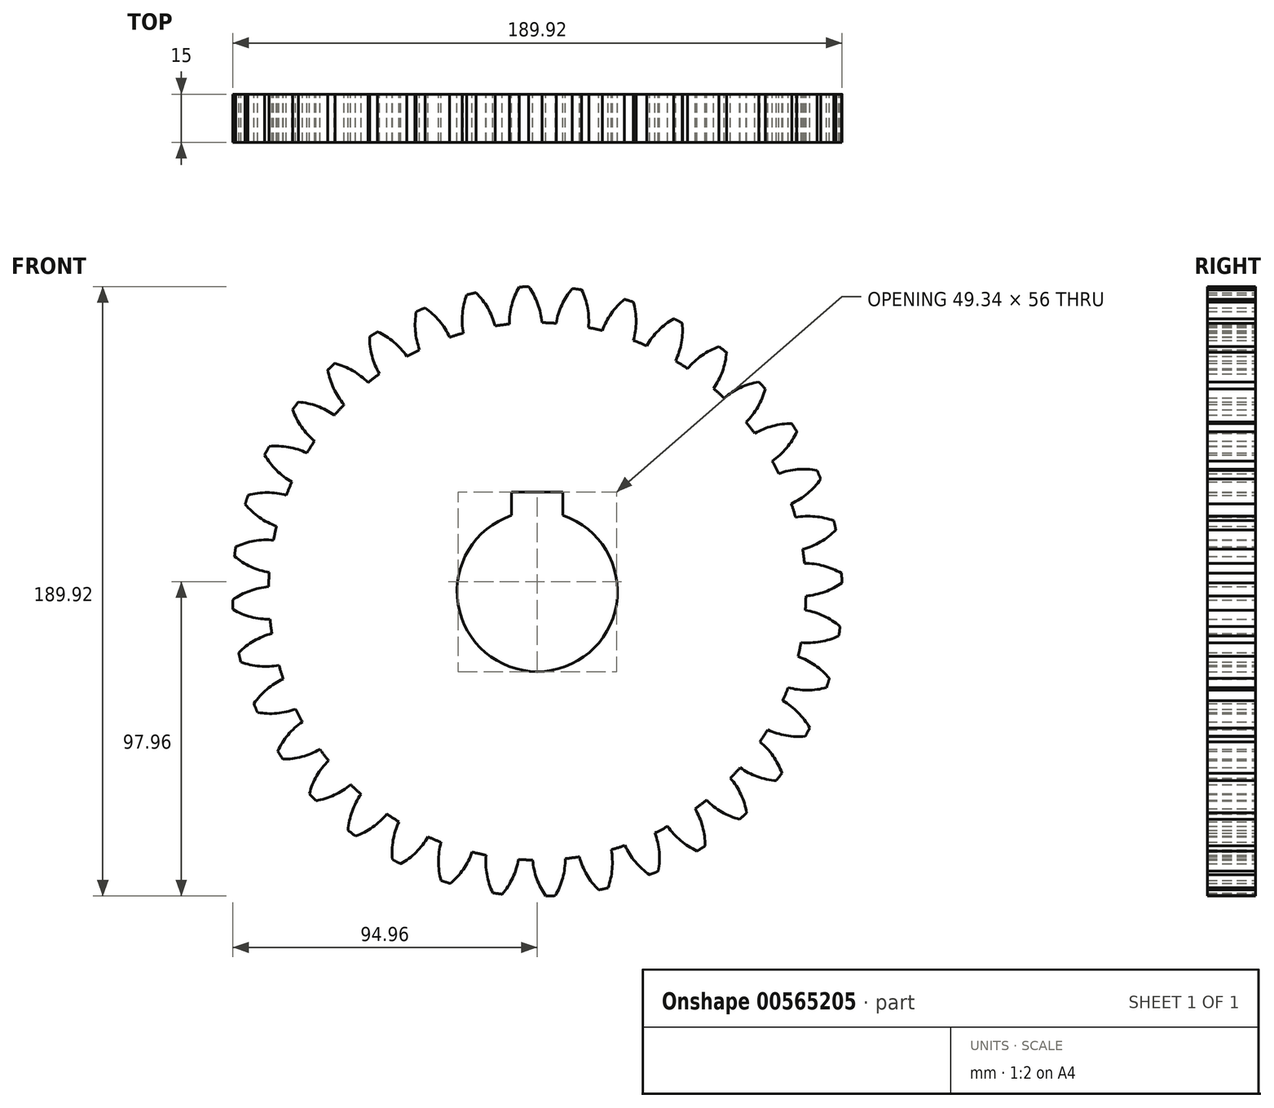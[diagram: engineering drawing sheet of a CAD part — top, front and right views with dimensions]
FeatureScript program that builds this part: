
annotation { "Feature Type Name" : "Feature", "Feature Type Description" : "" }
export const myFeature = defineFeature(function(context is Context, id is Id, definition is map)
    precondition{}
    {
        {
            var Q0;
            Q0=qCreatedBy(makeId("Front.planeOp"),FACE);
            var sketch = newSketch(context, id + "F0", { "sketchPlane" : qUnion([Q0])});
            skCircle(sketch, "E0", {"center": v(0, 0) * mm, "radius": 83.75 * mm});
            skCircle(sketch, "E1", {"center": v(0, 0) * mm, "radius": 90 * mm, "construction": true});
            skCircle(sketch, "E2", {"center": v(0, 0) * mm, "radius": 95 * mm, "construction": true});
            skLineSegment(sketch, "E3", {"start": v(0, 0) * mm, "end": v(0, 97.65) * mm, "construction": true});
            skLineSegment(sketch, "E4", {"start": v(0, 0) * mm, "end": v(-7.83, 179.33) * mm, "construction": true});
            skLineSegment(sketch, "E5", {"start": v(0, 90) * mm, "end": v(-217.65, 90) * mm, "construction": true});
            skLineSegment(sketch, "E6", {"start": v(0, 90) * mm, "end": v(-200.71, 16.95) * mm, "construction": true});
            skCircle(sketch, "E7", {"center": v(0, 0) * mm, "radius": 84.57 * mm, "construction": true});
            skCircle(sketch, "E8", {"center": v(0, 90) * mm, "radius": 22.5 * mm, "construction": true});
            skArc(sketch, "E9", {"start": v(0, 90) * mm, "mid": v(-1.18, 92.57) * mm, "end": v(-2.66, 94.96) * mm});
            skArc(sketch, "E10", {"start": v(1.43, 83.74) * mm, "mid": v(0.94, 86.92) * mm, "end": v(0, 90) * mm});
            skArc(sketch, "E11.MirrorCS", {"start": v(-8.72, 83.3) * mm, "mid": v(-8.5, 86.5) * mm, "end": v(-7.84, 89.66) * mm});
            skArc(sketch, "E12.MirrorCS", {"start": v(-7.84, 89.66) * mm, "mid": v(-6.9, 92.32) * mm, "end": v(-5.62, 94.83) * mm});
            skArc(sketch, "E13", {"start": v(-5.62, 94.83) * mm, "mid": v(-4.14, 94.9) * mm, "end": v(-2.66, 94.96) * mm});
            skSolve(sketch);
        }
        {
            var Q0;
            Q0=qSketchRegion(id+"F0",true);
            extrude(context, id + "F1", {"entities" : qUnion([Q0]), "depth" : 15 * mm, "offsetDistance" : 25.4 * mm});
        }
        {
            var Q0;
            Q0=makeQuery(id+"F1.opExtrude","SWEPT_BODY",BODY,{"disambiguationData":[OSD([sQuery(id+"F0.wireOp",EDGE,"E0"),sQuery(id+"F0.wireOp",EDGE,"E9"),sQuery(id+"F0.wireOp",EDGE,"E10"),sQuery(id+"F0.wireOp",EDGE,"E11.MirrorCS"),sQuery(id+"F0.wireOp",EDGE,"E12.MirrorCS"),sQuery(id+"F0.wireOp",EDGE,"E13")])]});
            var Q1;
            Q1=makeQuery(id+"F1.opExtrude","SWEPT_FACE",FACE,{"disambiguationData":[OSD([sQuery(id+"F0.wireOp",EDGE,"E0")])]});
            circularPattern(context, id + "F2", {"entities" : qUnion([Q0]), "axis" : qUnion([Q1]), "angle" : 360 * degree, "instanceCount" : 36, "equalSpace" : true});
        }
        {
            var Q0;
            Q0=makeQuery(id+"F2.opPattern","COPY",BODY,{"derivedFrom":makeQuery(id+"F1.opExtrude","SWEPT_BODY",BODY,{"disambiguationData":[OSD([sQuery(id+"F0.wireOp",EDGE,"E0"),sQuery(id+"F0.wireOp",EDGE,"E9"),sQuery(id+"F0.wireOp",EDGE,"E10"),sQuery(id+"F0.wireOp",EDGE,"E11.MirrorCS"),sQuery(id+"F0.wireOp",EDGE,"E12.MirrorCS"),sQuery(id+"F0.wireOp",EDGE,"E13")])]}),"instanceName":"17"});
            var Q1;
            Q1=makeQuery(id+"F2.opPattern","COPY",BODY,{"derivedFrom":makeQuery(id+"F1.opExtrude","SWEPT_BODY",BODY,{"disambiguationData":[OSD([sQuery(id+"F0.wireOp",EDGE,"E0"),sQuery(id+"F0.wireOp",EDGE,"E9"),sQuery(id+"F0.wireOp",EDGE,"E10"),sQuery(id+"F0.wireOp",EDGE,"E11.MirrorCS"),sQuery(id+"F0.wireOp",EDGE,"E12.MirrorCS"),sQuery(id+"F0.wireOp",EDGE,"E13")])]}),"instanceName":"13"});
            var Q2;
            Q2=makeQuery(id+"F1.opExtrude","SWEPT_BODY",BODY,{"disambiguationData":[OSD([sQuery(id+"F0.wireOp",EDGE,"E0"),sQuery(id+"F0.wireOp",EDGE,"E9"),sQuery(id+"F0.wireOp",EDGE,"E10"),sQuery(id+"F0.wireOp",EDGE,"E11.MirrorCS"),sQuery(id+"F0.wireOp",EDGE,"E12.MirrorCS"),sQuery(id+"F0.wireOp",EDGE,"E13")])]});
            var Q3;
            Q3=makeQuery(id+"F2.opPattern","COPY",BODY,{"derivedFrom":makeQuery(id+"F1.opExtrude","SWEPT_BODY",BODY,{"disambiguationData":[OSD([sQuery(id+"F0.wireOp",EDGE,"E0"),sQuery(id+"F0.wireOp",EDGE,"E9"),sQuery(id+"F0.wireOp",EDGE,"E10"),sQuery(id+"F0.wireOp",EDGE,"E11.MirrorCS"),sQuery(id+"F0.wireOp",EDGE,"E12.MirrorCS"),sQuery(id+"F0.wireOp",EDGE,"E13")])]}),"instanceName":"7"});
            var Q4;
            Q4=makeQuery(id+"F2.opPattern","COPY",BODY,{"derivedFrom":makeQuery(id+"F1.opExtrude","SWEPT_BODY",BODY,{"disambiguationData":[OSD([sQuery(id+"F0.wireOp",EDGE,"E0"),sQuery(id+"F0.wireOp",EDGE,"E9"),sQuery(id+"F0.wireOp",EDGE,"E10"),sQuery(id+"F0.wireOp",EDGE,"E11.MirrorCS"),sQuery(id+"F0.wireOp",EDGE,"E12.MirrorCS"),sQuery(id+"F0.wireOp",EDGE,"E13")])]}),"instanceName":"18"});
            var Q5;
            Q5=makeQuery(id+"F2.opPattern","COPY",BODY,{"derivedFrom":makeQuery(id+"F1.opExtrude","SWEPT_BODY",BODY,{"disambiguationData":[OSD([sQuery(id+"F0.wireOp",EDGE,"E0"),sQuery(id+"F0.wireOp",EDGE,"E9"),sQuery(id+"F0.wireOp",EDGE,"E10"),sQuery(id+"F0.wireOp",EDGE,"E11.MirrorCS"),sQuery(id+"F0.wireOp",EDGE,"E12.MirrorCS"),sQuery(id+"F0.wireOp",EDGE,"E13")])]}),"instanceName":"3"});
            var Q6;
            Q6=makeQuery(id+"F2.opPattern","COPY",BODY,{"derivedFrom":makeQuery(id+"F1.opExtrude","SWEPT_BODY",BODY,{"disambiguationData":[OSD([sQuery(id+"F0.wireOp",EDGE,"E0"),sQuery(id+"F0.wireOp",EDGE,"E9"),sQuery(id+"F0.wireOp",EDGE,"E10"),sQuery(id+"F0.wireOp",EDGE,"E11.MirrorCS"),sQuery(id+"F0.wireOp",EDGE,"E12.MirrorCS"),sQuery(id+"F0.wireOp",EDGE,"E13")])]}),"instanceName":"16"});
            var Q7;
            Q7=makeQuery(id+"F2.opPattern","COPY",BODY,{"derivedFrom":makeQuery(id+"F1.opExtrude","SWEPT_BODY",BODY,{"disambiguationData":[OSD([sQuery(id+"F0.wireOp",EDGE,"E0"),sQuery(id+"F0.wireOp",EDGE,"E9"),sQuery(id+"F0.wireOp",EDGE,"E10"),sQuery(id+"F0.wireOp",EDGE,"E11.MirrorCS"),sQuery(id+"F0.wireOp",EDGE,"E12.MirrorCS"),sQuery(id+"F0.wireOp",EDGE,"E13")])]}),"instanceName":"8"});
            var Q8;
            Q8=makeQuery(id+"F2.opPattern","COPY",BODY,{"derivedFrom":makeQuery(id+"F1.opExtrude","SWEPT_BODY",BODY,{"disambiguationData":[OSD([sQuery(id+"F0.wireOp",EDGE,"E0"),sQuery(id+"F0.wireOp",EDGE,"E9"),sQuery(id+"F0.wireOp",EDGE,"E10"),sQuery(id+"F0.wireOp",EDGE,"E11.MirrorCS"),sQuery(id+"F0.wireOp",EDGE,"E12.MirrorCS"),sQuery(id+"F0.wireOp",EDGE,"E13")])]}),"instanceName":"19"});
            var Q9;
            Q9=makeQuery(id+"F2.opPattern","COPY",BODY,{"derivedFrom":makeQuery(id+"F1.opExtrude","SWEPT_BODY",BODY,{"disambiguationData":[OSD([sQuery(id+"F0.wireOp",EDGE,"E0"),sQuery(id+"F0.wireOp",EDGE,"E9"),sQuery(id+"F0.wireOp",EDGE,"E10"),sQuery(id+"F0.wireOp",EDGE,"E11.MirrorCS"),sQuery(id+"F0.wireOp",EDGE,"E12.MirrorCS"),sQuery(id+"F0.wireOp",EDGE,"E13")])]}),"instanceName":"1"});
            var Q10;
            Q10=makeQuery(id+"F2.opPattern","COPY",BODY,{"derivedFrom":makeQuery(id+"F1.opExtrude","SWEPT_BODY",BODY,{"disambiguationData":[OSD([sQuery(id+"F0.wireOp",EDGE,"E0"),sQuery(id+"F0.wireOp",EDGE,"E9"),sQuery(id+"F0.wireOp",EDGE,"E10"),sQuery(id+"F0.wireOp",EDGE,"E11.MirrorCS"),sQuery(id+"F0.wireOp",EDGE,"E12.MirrorCS"),sQuery(id+"F0.wireOp",EDGE,"E13")])]}),"instanceName":"34"});
            var Q11;
            Q11=makeQuery(id+"F2.opPattern","COPY",BODY,{"derivedFrom":makeQuery(id+"F1.opExtrude","SWEPT_BODY",BODY,{"disambiguationData":[OSD([sQuery(id+"F0.wireOp",EDGE,"E0"),sQuery(id+"F0.wireOp",EDGE,"E9"),sQuery(id+"F0.wireOp",EDGE,"E10"),sQuery(id+"F0.wireOp",EDGE,"E11.MirrorCS"),sQuery(id+"F0.wireOp",EDGE,"E12.MirrorCS"),sQuery(id+"F0.wireOp",EDGE,"E13")])]}),"instanceName":"33"});
            var Q12;
            Q12=makeQuery(id+"F2.opPattern","COPY",BODY,{"derivedFrom":makeQuery(id+"F1.opExtrude","SWEPT_BODY",BODY,{"disambiguationData":[OSD([sQuery(id+"F0.wireOp",EDGE,"E0"),sQuery(id+"F0.wireOp",EDGE,"E9"),sQuery(id+"F0.wireOp",EDGE,"E10"),sQuery(id+"F0.wireOp",EDGE,"E11.MirrorCS"),sQuery(id+"F0.wireOp",EDGE,"E12.MirrorCS"),sQuery(id+"F0.wireOp",EDGE,"E13")])]}),"instanceName":"32"});
            var Q13;
            Q13=makeQuery(id+"F2.opPattern","COPY",BODY,{"derivedFrom":makeQuery(id+"F1.opExtrude","SWEPT_BODY",BODY,{"disambiguationData":[OSD([sQuery(id+"F0.wireOp",EDGE,"E0"),sQuery(id+"F0.wireOp",EDGE,"E9"),sQuery(id+"F0.wireOp",EDGE,"E10"),sQuery(id+"F0.wireOp",EDGE,"E11.MirrorCS"),sQuery(id+"F0.wireOp",EDGE,"E12.MirrorCS"),sQuery(id+"F0.wireOp",EDGE,"E13")])]}),"instanceName":"31"});
            var Q14;
            Q14=makeQuery(id+"F2.opPattern","COPY",BODY,{"derivedFrom":makeQuery(id+"F1.opExtrude","SWEPT_BODY",BODY,{"disambiguationData":[OSD([sQuery(id+"F0.wireOp",EDGE,"E0"),sQuery(id+"F0.wireOp",EDGE,"E9"),sQuery(id+"F0.wireOp",EDGE,"E10"),sQuery(id+"F0.wireOp",EDGE,"E11.MirrorCS"),sQuery(id+"F0.wireOp",EDGE,"E12.MirrorCS"),sQuery(id+"F0.wireOp",EDGE,"E13")])]}),"instanceName":"30"});
            var Q15;
            Q15=makeQuery(id+"F2.opPattern","COPY",BODY,{"derivedFrom":makeQuery(id+"F1.opExtrude","SWEPT_BODY",BODY,{"disambiguationData":[OSD([sQuery(id+"F0.wireOp",EDGE,"E0"),sQuery(id+"F0.wireOp",EDGE,"E9"),sQuery(id+"F0.wireOp",EDGE,"E10"),sQuery(id+"F0.wireOp",EDGE,"E11.MirrorCS"),sQuery(id+"F0.wireOp",EDGE,"E12.MirrorCS"),sQuery(id+"F0.wireOp",EDGE,"E13")])]}),"instanceName":"29"});
            var Q16;
            Q16=makeQuery(id+"F2.opPattern","COPY",BODY,{"derivedFrom":makeQuery(id+"F1.opExtrude","SWEPT_BODY",BODY,{"disambiguationData":[OSD([sQuery(id+"F0.wireOp",EDGE,"E0"),sQuery(id+"F0.wireOp",EDGE,"E9"),sQuery(id+"F0.wireOp",EDGE,"E10"),sQuery(id+"F0.wireOp",EDGE,"E11.MirrorCS"),sQuery(id+"F0.wireOp",EDGE,"E12.MirrorCS"),sQuery(id+"F0.wireOp",EDGE,"E13")])]}),"instanceName":"28"});
            var Q17;
            Q17=makeQuery(id+"F2.opPattern","COPY",BODY,{"derivedFrom":makeQuery(id+"F1.opExtrude","SWEPT_BODY",BODY,{"disambiguationData":[OSD([sQuery(id+"F0.wireOp",EDGE,"E0"),sQuery(id+"F0.wireOp",EDGE,"E9"),sQuery(id+"F0.wireOp",EDGE,"E10"),sQuery(id+"F0.wireOp",EDGE,"E11.MirrorCS"),sQuery(id+"F0.wireOp",EDGE,"E12.MirrorCS"),sQuery(id+"F0.wireOp",EDGE,"E13")])]}),"instanceName":"27"});
            var Q18;
            Q18=makeQuery(id+"F2.opPattern","COPY",BODY,{"derivedFrom":makeQuery(id+"F1.opExtrude","SWEPT_BODY",BODY,{"disambiguationData":[OSD([sQuery(id+"F0.wireOp",EDGE,"E0"),sQuery(id+"F0.wireOp",EDGE,"E9"),sQuery(id+"F0.wireOp",EDGE,"E10"),sQuery(id+"F0.wireOp",EDGE,"E11.MirrorCS"),sQuery(id+"F0.wireOp",EDGE,"E12.MirrorCS"),sQuery(id+"F0.wireOp",EDGE,"E13")])]}),"instanceName":"26"});
            var Q19;
            Q19=makeQuery(id+"F2.opPattern","COPY",BODY,{"derivedFrom":makeQuery(id+"F1.opExtrude","SWEPT_BODY",BODY,{"disambiguationData":[OSD([sQuery(id+"F0.wireOp",EDGE,"E0"),sQuery(id+"F0.wireOp",EDGE,"E9"),sQuery(id+"F0.wireOp",EDGE,"E10"),sQuery(id+"F0.wireOp",EDGE,"E11.MirrorCS"),sQuery(id+"F0.wireOp",EDGE,"E12.MirrorCS"),sQuery(id+"F0.wireOp",EDGE,"E13")])]}),"instanceName":"25"});
            var Q20;
            Q20=makeQuery(id+"F2.opPattern","COPY",BODY,{"derivedFrom":makeQuery(id+"F1.opExtrude","SWEPT_BODY",BODY,{"disambiguationData":[OSD([sQuery(id+"F0.wireOp",EDGE,"E0"),sQuery(id+"F0.wireOp",EDGE,"E9"),sQuery(id+"F0.wireOp",EDGE,"E10"),sQuery(id+"F0.wireOp",EDGE,"E11.MirrorCS"),sQuery(id+"F0.wireOp",EDGE,"E12.MirrorCS"),sQuery(id+"F0.wireOp",EDGE,"E13")])]}),"instanceName":"23"});
            var Q21;
            Q21=makeQuery(id+"F2.opPattern","COPY",BODY,{"derivedFrom":makeQuery(id+"F1.opExtrude","SWEPT_BODY",BODY,{"disambiguationData":[OSD([sQuery(id+"F0.wireOp",EDGE,"E0"),sQuery(id+"F0.wireOp",EDGE,"E9"),sQuery(id+"F0.wireOp",EDGE,"E10"),sQuery(id+"F0.wireOp",EDGE,"E11.MirrorCS"),sQuery(id+"F0.wireOp",EDGE,"E12.MirrorCS"),sQuery(id+"F0.wireOp",EDGE,"E13")])]}),"instanceName":"5"});
            var Q22;
            Q22=makeQuery(id+"F2.opPattern","COPY",BODY,{"derivedFrom":makeQuery(id+"F1.opExtrude","SWEPT_BODY",BODY,{"disambiguationData":[OSD([sQuery(id+"F0.wireOp",EDGE,"E0"),sQuery(id+"F0.wireOp",EDGE,"E9"),sQuery(id+"F0.wireOp",EDGE,"E10"),sQuery(id+"F0.wireOp",EDGE,"E11.MirrorCS"),sQuery(id+"F0.wireOp",EDGE,"E12.MirrorCS"),sQuery(id+"F0.wireOp",EDGE,"E13")])]}),"instanceName":"2"});
            var Q23;
            Q23=makeQuery(id+"F2.opPattern","COPY",BODY,{"derivedFrom":makeQuery(id+"F1.opExtrude","SWEPT_BODY",BODY,{"disambiguationData":[OSD([sQuery(id+"F0.wireOp",EDGE,"E0"),sQuery(id+"F0.wireOp",EDGE,"E9"),sQuery(id+"F0.wireOp",EDGE,"E10"),sQuery(id+"F0.wireOp",EDGE,"E11.MirrorCS"),sQuery(id+"F0.wireOp",EDGE,"E12.MirrorCS"),sQuery(id+"F0.wireOp",EDGE,"E13")])]}),"instanceName":"9"});
            var Q24;
            Q24=makeQuery(id+"F2.opPattern","COPY",BODY,{"derivedFrom":makeQuery(id+"F1.opExtrude","SWEPT_BODY",BODY,{"disambiguationData":[OSD([sQuery(id+"F0.wireOp",EDGE,"E0"),sQuery(id+"F0.wireOp",EDGE,"E9"),sQuery(id+"F0.wireOp",EDGE,"E10"),sQuery(id+"F0.wireOp",EDGE,"E11.MirrorCS"),sQuery(id+"F0.wireOp",EDGE,"E12.MirrorCS"),sQuery(id+"F0.wireOp",EDGE,"E13")])]}),"instanceName":"22"});
            var Q25;
            Q25=makeQuery(id+"F2.opPattern","COPY",BODY,{"derivedFrom":makeQuery(id+"F1.opExtrude","SWEPT_BODY",BODY,{"disambiguationData":[OSD([sQuery(id+"F0.wireOp",EDGE,"E0"),sQuery(id+"F0.wireOp",EDGE,"E9"),sQuery(id+"F0.wireOp",EDGE,"E10"),sQuery(id+"F0.wireOp",EDGE,"E11.MirrorCS"),sQuery(id+"F0.wireOp",EDGE,"E12.MirrorCS"),sQuery(id+"F0.wireOp",EDGE,"E13")])]}),"instanceName":"24"});
            var Q26;
            Q26=makeQuery(id+"F2.opPattern","COPY",BODY,{"derivedFrom":makeQuery(id+"F1.opExtrude","SWEPT_BODY",BODY,{"disambiguationData":[OSD([sQuery(id+"F0.wireOp",EDGE,"E0"),sQuery(id+"F0.wireOp",EDGE,"E9"),sQuery(id+"F0.wireOp",EDGE,"E10"),sQuery(id+"F0.wireOp",EDGE,"E11.MirrorCS"),sQuery(id+"F0.wireOp",EDGE,"E12.MirrorCS"),sQuery(id+"F0.wireOp",EDGE,"E13")])]}),"instanceName":"35"});
            var Q27;
            Q27=makeQuery(id+"F2.opPattern","COPY",BODY,{"derivedFrom":makeQuery(id+"F1.opExtrude","SWEPT_BODY",BODY,{"disambiguationData":[OSD([sQuery(id+"F0.wireOp",EDGE,"E0"),sQuery(id+"F0.wireOp",EDGE,"E9"),sQuery(id+"F0.wireOp",EDGE,"E10"),sQuery(id+"F0.wireOp",EDGE,"E11.MirrorCS"),sQuery(id+"F0.wireOp",EDGE,"E12.MirrorCS"),sQuery(id+"F0.wireOp",EDGE,"E13")])]}),"instanceName":"12"});
            var Q28;
            Q28=makeQuery(id+"F2.opPattern","COPY",BODY,{"derivedFrom":makeQuery(id+"F1.opExtrude","SWEPT_BODY",BODY,{"disambiguationData":[OSD([sQuery(id+"F0.wireOp",EDGE,"E0"),sQuery(id+"F0.wireOp",EDGE,"E9"),sQuery(id+"F0.wireOp",EDGE,"E10"),sQuery(id+"F0.wireOp",EDGE,"E11.MirrorCS"),sQuery(id+"F0.wireOp",EDGE,"E12.MirrorCS"),sQuery(id+"F0.wireOp",EDGE,"E13")])]}),"instanceName":"10"});
            var Q29;
            Q29=makeQuery(id+"F2.opPattern","COPY",BODY,{"derivedFrom":makeQuery(id+"F1.opExtrude","SWEPT_BODY",BODY,{"disambiguationData":[OSD([sQuery(id+"F0.wireOp",EDGE,"E0"),sQuery(id+"F0.wireOp",EDGE,"E9"),sQuery(id+"F0.wireOp",EDGE,"E10"),sQuery(id+"F0.wireOp",EDGE,"E11.MirrorCS"),sQuery(id+"F0.wireOp",EDGE,"E12.MirrorCS"),sQuery(id+"F0.wireOp",EDGE,"E13")])]}),"instanceName":"6"});
            var Q30;
            Q30=makeQuery(id+"F2.opPattern","COPY",BODY,{"derivedFrom":makeQuery(id+"F1.opExtrude","SWEPT_BODY",BODY,{"disambiguationData":[OSD([sQuery(id+"F0.wireOp",EDGE,"E0"),sQuery(id+"F0.wireOp",EDGE,"E9"),sQuery(id+"F0.wireOp",EDGE,"E10"),sQuery(id+"F0.wireOp",EDGE,"E11.MirrorCS"),sQuery(id+"F0.wireOp",EDGE,"E12.MirrorCS"),sQuery(id+"F0.wireOp",EDGE,"E13")])]}),"instanceName":"11"});
            var Q31;
            Q31=makeQuery(id+"F2.opPattern","COPY",BODY,{"derivedFrom":makeQuery(id+"F1.opExtrude","SWEPT_BODY",BODY,{"disambiguationData":[OSD([sQuery(id+"F0.wireOp",EDGE,"E0"),sQuery(id+"F0.wireOp",EDGE,"E9"),sQuery(id+"F0.wireOp",EDGE,"E10"),sQuery(id+"F0.wireOp",EDGE,"E11.MirrorCS"),sQuery(id+"F0.wireOp",EDGE,"E12.MirrorCS"),sQuery(id+"F0.wireOp",EDGE,"E13")])]}),"instanceName":"14"});
            var Q32;
            Q32=makeQuery(id+"F2.opPattern","COPY",BODY,{"derivedFrom":makeQuery(id+"F1.opExtrude","SWEPT_BODY",BODY,{"disambiguationData":[OSD([sQuery(id+"F0.wireOp",EDGE,"E0"),sQuery(id+"F0.wireOp",EDGE,"E9"),sQuery(id+"F0.wireOp",EDGE,"E10"),sQuery(id+"F0.wireOp",EDGE,"E11.MirrorCS"),sQuery(id+"F0.wireOp",EDGE,"E12.MirrorCS"),sQuery(id+"F0.wireOp",EDGE,"E13")])]}),"instanceName":"4"});
            var Q33;
            Q33=makeQuery(id+"F2.opPattern","COPY",BODY,{"derivedFrom":makeQuery(id+"F1.opExtrude","SWEPT_BODY",BODY,{"disambiguationData":[OSD([sQuery(id+"F0.wireOp",EDGE,"E0"),sQuery(id+"F0.wireOp",EDGE,"E9"),sQuery(id+"F0.wireOp",EDGE,"E10"),sQuery(id+"F0.wireOp",EDGE,"E11.MirrorCS"),sQuery(id+"F0.wireOp",EDGE,"E12.MirrorCS"),sQuery(id+"F0.wireOp",EDGE,"E13")])]}),"instanceName":"21"});
            var Q34;
            Q34=makeQuery(id+"F2.opPattern","COPY",BODY,{"derivedFrom":makeQuery(id+"F1.opExtrude","SWEPT_BODY",BODY,{"disambiguationData":[OSD([sQuery(id+"F0.wireOp",EDGE,"E0"),sQuery(id+"F0.wireOp",EDGE,"E9"),sQuery(id+"F0.wireOp",EDGE,"E10"),sQuery(id+"F0.wireOp",EDGE,"E11.MirrorCS"),sQuery(id+"F0.wireOp",EDGE,"E12.MirrorCS"),sQuery(id+"F0.wireOp",EDGE,"E13")])]}),"instanceName":"20"});
            var Q35;
            Q35=makeQuery(id+"F2.opPattern","COPY",BODY,{"derivedFrom":makeQuery(id+"F1.opExtrude","SWEPT_BODY",BODY,{"disambiguationData":[OSD([sQuery(id+"F0.wireOp",EDGE,"E0"),sQuery(id+"F0.wireOp",EDGE,"E9"),sQuery(id+"F0.wireOp",EDGE,"E10"),sQuery(id+"F0.wireOp",EDGE,"E11.MirrorCS"),sQuery(id+"F0.wireOp",EDGE,"E12.MirrorCS"),sQuery(id+"F0.wireOp",EDGE,"E13")])]}),"instanceName":"15"});
            booleanBodies(context, id + "F3", {"operationType" : BooleanOperationType.UNION, "tools" : qUnion([Q0, Q1, Q2, Q3, Q4, Q5, Q6, Q7, Q8, Q9, Q10, Q11, Q12, Q13, Q14, Q15, Q16, Q17, Q18, Q19, Q20, Q21, Q22, Q23, Q24, Q25, Q26, Q27, Q28, Q29, Q30, Q31, Q32, Q33, Q34, Q35])});
        }
        {
            var Q0;
            {var subQ0=makeQuery(id+"F1.opExtrude","CAP_FACE",FACE,{"disambiguationData":[OSD([sQuery(id+"F0.wireOp",EDGE,"E0"),sQuery(id+"F0.wireOp",EDGE,"E9"),sQuery(id+"F0.wireOp",EDGE,"E10"),sQuery(id+"F0.wireOp",EDGE,"E11.MirrorCS"),sQuery(id+"F0.wireOp",EDGE,"E12.MirrorCS"),sQuery(id+"F0.wireOp",EDGE,"E13")])],"isStart":true});Q0=makeQuery(id+"F3.opBoolean","MERGE",FACE,{"derivedFrom":[subQ0,makeQuery(id+"F2.opPattern","COPY",FACE,{"derivedFrom":subQ0,"instanceName":"1"}),makeQuery(id+"F2.opPattern","COPY",FACE,{"derivedFrom":subQ0,"instanceName":"2"}),makeQuery(id+"F2.opPattern","COPY",FACE,{"derivedFrom":subQ0,"instanceName":"3"}),makeQuery(id+"F2.opPattern","COPY",FACE,{"derivedFrom":subQ0,"instanceName":"4"}),makeQuery(id+"F2.opPattern","COPY",FACE,{"derivedFrom":subQ0,"instanceName":"5"}),makeQuery(id+"F2.opPattern","COPY",FACE,{"derivedFrom":subQ0,"instanceName":"6"}),makeQuery(id+"F2.opPattern","COPY",FACE,{"derivedFrom":subQ0,"instanceName":"7"}),makeQuery(id+"F2.opPattern","COPY",FACE,{"derivedFrom":subQ0,"instanceName":"8"}),makeQuery(id+"F2.opPattern","COPY",FACE,{"derivedFrom":subQ0,"instanceName":"9"}),makeQuery(id+"F2.opPattern","COPY",FACE,{"derivedFrom":subQ0,"instanceName":"10"}),makeQuery(id+"F2.opPattern","COPY",FACE,{"derivedFrom":subQ0,"instanceName":"11"}),makeQuery(id+"F2.opPattern","COPY",FACE,{"derivedFrom":subQ0,"instanceName":"12"}),makeQuery(id+"F2.opPattern","COPY",FACE,{"derivedFrom":subQ0,"instanceName":"13"}),makeQuery(id+"F2.opPattern","COPY",FACE,{"derivedFrom":subQ0,"instanceName":"14"}),makeQuery(id+"F2.opPattern","COPY",FACE,{"derivedFrom":subQ0,"instanceName":"15"}),makeQuery(id+"F2.opPattern","COPY",FACE,{"derivedFrom":subQ0,"instanceName":"16"}),makeQuery(id+"F2.opPattern","COPY",FACE,{"derivedFrom":subQ0,"instanceName":"17"}),makeQuery(id+"F2.opPattern","COPY",FACE,{"derivedFrom":subQ0,"instanceName":"18"}),makeQuery(id+"F2.opPattern","COPY",FACE,{"derivedFrom":subQ0,"instanceName":"19"}),makeQuery(id+"F2.opPattern","COPY",FACE,{"derivedFrom":subQ0,"instanceName":"20"}),makeQuery(id+"F2.opPattern","COPY",FACE,{"derivedFrom":subQ0,"instanceName":"21"}),makeQuery(id+"F2.opPattern","COPY",FACE,{"derivedFrom":subQ0,"instanceName":"22"}),makeQuery(id+"F2.opPattern","COPY",FACE,{"derivedFrom":subQ0,"instanceName":"23"}),makeQuery(id+"F2.opPattern","COPY",FACE,{"derivedFrom":subQ0,"instanceName":"24"}),makeQuery(id+"F2.opPattern","COPY",FACE,{"derivedFrom":subQ0,"instanceName":"25"}),makeQuery(id+"F2.opPattern","COPY",FACE,{"derivedFrom":subQ0,"instanceName":"26"}),makeQuery(id+"F2.opPattern","COPY",FACE,{"derivedFrom":subQ0,"instanceName":"27"}),makeQuery(id+"F2.opPattern","COPY",FACE,{"derivedFrom":subQ0,"instanceName":"28"}),makeQuery(id+"F2.opPattern","COPY",FACE,{"derivedFrom":subQ0,"instanceName":"29"}),makeQuery(id+"F2.opPattern","COPY",FACE,{"derivedFrom":subQ0,"instanceName":"30"}),makeQuery(id+"F2.opPattern","COPY",FACE,{"derivedFrom":subQ0,"instanceName":"31"}),makeQuery(id+"F2.opPattern","COPY",FACE,{"derivedFrom":subQ0,"instanceName":"32"}),makeQuery(id+"F2.opPattern","COPY",FACE,{"derivedFrom":subQ0,"instanceName":"33"}),makeQuery(id+"F2.opPattern","COPY",FACE,{"derivedFrom":subQ0,"instanceName":"34"}),makeQuery(id+"F2.opPattern","COPY",FACE,{"derivedFrom":subQ0,"instanceName":"35"})]});}
            var sketch = newSketch(context, id + "F4", { "sketchPlane" : qUnion([Q0])});
            skCircle(sketch, "E14", {"center": v(0, 0) * mm, "radius": 25 * mm});
            skLineSegment(sketch, "E15.bottom", {"start": v(-8, 31) * mm, "end": v(8, 31) * mm});
            skLineSegment(sketch, "E15.top", {"start": v(-8, 19) * mm, "end": v(8, 19) * mm});
            skLineSegment(sketch, "E15.left", {"start": v(-8, 31) * mm, "end": v(-8, 19) * mm});
            skLineSegment(sketch, "E15.right", {"start": v(8, 31) * mm, "end": v(8, 19) * mm});
            skSolve(sketch);
        }
        {
            var Q0;
            Q0=qSketchRegion(id+"F4",true);
            extrude(context, id + "F5", {"entities" : qUnion([Q0]), "operationType" : NewBodyOperationType.REMOVE, "oppositeDirection" : true, "depth" : 25.4 * mm, "offsetDistance" : 25.4 * mm});
        }
    });
